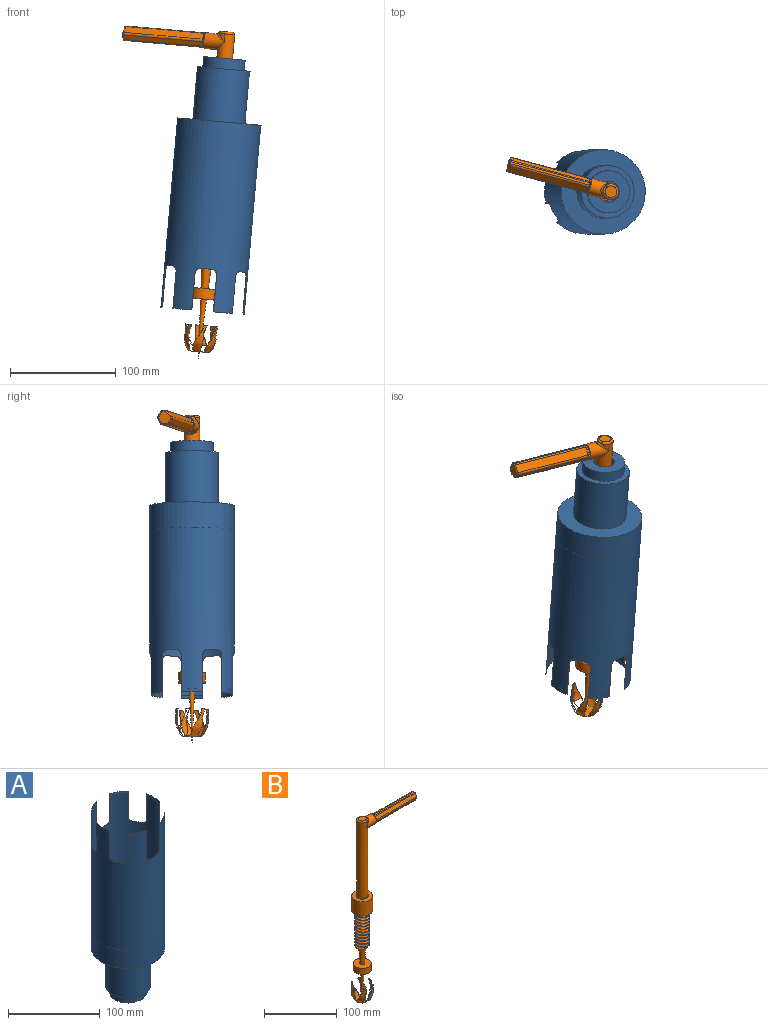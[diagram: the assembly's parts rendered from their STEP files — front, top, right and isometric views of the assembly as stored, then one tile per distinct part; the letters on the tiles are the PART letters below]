
ASSEMBLY  parts=2 mates=1
PART A: 54 faces, bbox 93.2x90.1x245.5 mm
  f0: plane 51.91x51.91mm, normal (0,0,1), area 1606.4mm2, adj f42,f44,f46,f47
  f1: cylinder r=39.5mm len=153.01mm, axis (0,0,-1), area 33532.5mm2, adj f4,f5,f6,f7,f8,f9,f10,f11
  f2: cylinder r=40mm len=180mm, axis (0,0,-1), area 40362.7mm2, adj f3,f4,f5,f6,f7,f8,f9,f10
  f3: plane 80x80mm, normal (0,0,-1), area 3063mm2, adj f2,f48
  f4: plane 35x0.35mm, normal (0.71,-0.71,0), area 17mm2, adj f1,f2,f25,f34
  f5: plane 35x0.48mm, normal (-0.26,0.97,0), area 17mm2, adj f1,f2,f26,f35
  f6: plane 9.56x5.8mm, normal (0,0,1), area 5.4mm2, adj f1,f2,f34,f35
  f7: plane 35x0.48mm, normal (-0.26,-0.97,0), area 17mm2, adj f1,f2,f26,f36
  f8: plane 35x0.35mm, normal (0.71,0.71,0), area 17mm2, adj f1,f2,f22,f37
  f9: plane 9.56x5.8mm, normal (0,0,1), area 5.4mm2, adj f1,f2,f36,f37
  f10: plane 35x0.48mm, normal (-0.97,-0.26,0), area 17mm2, adj f1,f2,f22,f38
  f11: plane 35x0.48mm, normal (0.97,-0.26,0), area 17mm2, adj f1,f2,f23,f39
  f12: plane 10.88x0.86mm, normal (0,0,1), area 5.4mm2, adj f1,f2,f38,f39
  f13: plane 35x0.35mm, normal (-0.71,0.71,0), area 17mm2, adj f1,f2,f23,f29
  f14: plane 35x0.48mm, normal (0.26,-0.97,0), area 17mm2, adj f1,f2,f27,f28
  f15: plane 9.56x5.8mm, normal (0,0,1), area 5.4mm2, adj f1,f2,f28,f29
  f16: plane 35x0.48mm, normal (0.26,0.97,0), area 17mm2, adj f1,f2,f27,f30
  f17: plane 35x0.35mm, normal (-0.71,-0.71,0), area 17mm2, adj f1,f2,f24,f31
  f18: plane 9.56x5.8mm, normal (0,0,1), area 5.4mm2, adj f1,f2,f30,f31
  f19: plane 35x0.48mm, normal (0.97,0.26,0), area 17mm2, adj f1,f2,f24,f32
  f20: plane 35x0.48mm, normal (-0.97,0.26,0), area 17mm2, adj f1,f2,f25,f33
  f21: plane 10.88x0.86mm, normal (0,0,1), area 5.4mm2, adj f1,f2,f32,f33
  f22: torus R=48.7mm, axis (0,0,1), area 63.3mm2, adj f1,f2,f8,f10
  f23: torus R=48.7mm, axis (0,0,1), area 63.3mm2, adj f1,f2,f11,f13
  f24: torus R=48.7mm, axis (0,0,1), area 63.3mm2, adj f1,f2,f17,f19
  f25: torus R=48.7mm, axis (0,0,1), area 63.3mm2, adj f1,f2,f4,f20
  f26: torus R=48.7mm, axis (0,0,1), area 63.3mm2, adj f1,f2,f5,f7
  f27: torus R=48.7mm, axis (0,0,1), area 63.3mm2, adj f1,f2,f14,f16
  f28: cylinder r=5mm len=5.04mm, axis (-0.97,-0.26,0), area 3.9mm2, adj f1,f2,f14,f15
  f29: cylinder r=5mm len=5mm, axis (0.71,0.71,0), area 3.9mm2, adj f1,f2,f13,f15
  f30: cylinder r=5mm len=5.04mm, axis (0.97,-0.26,0), area 3.9mm2, adj f1,f2,f16,f18
  f31: cylinder r=5mm len=5mm, axis (-0.71,0.71,0), area 3.9mm2, adj f1,f2,f17,f18
  f32: cylinder r=5mm len=5.04mm, axis (0.26,-0.97,0), area 3.9mm2, adj f1,f2,f19,f21
  f33: cylinder r=5mm len=5.04mm, axis (0.26,0.97,0), area 3.9mm2, adj f1,f2,f20,f21
  f34: cylinder r=5mm len=5mm, axis (-0.71,-0.71,0), area 3.9mm2, adj f1,f2,f4,f6
  f35: cylinder r=5mm len=5.04mm, axis (0.97,0.26,0), area 3.9mm2, adj f1,f2,f5,f6
  f36: cylinder r=5mm len=5.04mm, axis (-0.97,0.26,0), area 3.9mm2, adj f1,f2,f7,f9
  f37: cylinder r=5mm len=5mm, axis (0.71,-0.71,0), area 3.9mm2, adj f1,f2,f8,f9
  f38: cylinder r=5mm len=5.04mm, axis (-0.26,0.97,0), area 3.9mm2, adj f1,f2,f10,f12
  f39: cylinder r=5mm len=5.04mm, axis (-0.26,-0.97,0), area 3.9mm2, adj f1,f2,f11,f12
  f40: plane 79x79mm, normal (0,0,1), area 2938.2mm2, adj f1,f42
  f41: cylinder r=15mm len=74mm, axis (0,0,-1), area 6974.3mm2, adj f43,f52
  f42: cylinder r=25mm len=60mm, axis (0,0,-1), area 9424.8mm2, adj f0,f40
  f43: plane 31.91x31.91mm, normal (0,0,-1), area 349.8mm2, adj f41,f44,f45,f47
  f44: cylinder r=10mm len=60mm, axis (0,0,1), area 916.9mm2, adj f0,f43,f45,f46,f47
  f45: plane 2.57x2.57mm, normal (0,1,0), area 3.1mm2, adj f43,f44,f47
  f46: plane 2.57x2.57mm, normal (0,-1,0), area 3.1mm2, adj f0,f44,f47
  f47: bspline ~64x32.33mm, area 5274.5mm2, adj f0,f43,f44,f45,f46
  f48: cylinder r=25mm len=50mm, axis (0,0,1), area 7854mm2, adj f3,f49
  f49: plane 50x50mm, normal (0,0,-1), area 706.9mm2, adj f48,f50
  f50: cylinder r=20mm len=40mm, axis (0,0,1), area 1256.6mm2, adj f49,f51
  f51: plane 40x40mm, normal (0,0,-1), area 942.5mm2, adj f50,f53
  f52: plane 30x30mm, normal (0,0,1), area 392.7mm2, adj f41,f53
  f53: cylinder r=10mm len=20mm, axis (0,0,-1), area 628.3mm2, adj f51,f52
PART B: 83 faces, bbox 123x42.3x312.1 mm
  f0: cylinder r=10mm len=60mm, axis (0,0,1), area 916.9mm2, adj f1,f54,f55,f56,f82
  f1: plane 30.91x30.91mm, normal (0,0,-1), area 303.5mm2, adj f0,f2,f54,f55
  f2: cylinder r=14.5mm len=29mm, axis (0,0,-1), area 2186.5mm2, adj f1,f3
  f3: plane 29x29mm, normal (0,0,1), area 433.5mm2, adj f2,f4
  f4: torus R=8.5mm, axis (0,0,1), area 77.6mm2, adj f3,f5
  f5: cylinder r=7.5mm len=127mm, axis (0,0,-1), area 5698.8mm2, adj f4,f6,f7,f10,f52,f53
  f6: cylinder r=7.5mm len=8mm, axis (0,0,-1), area 30mm2, adj f5,f7,f10
  f7: torus R=5.5mm, axis (0,0,1), area 109.5mm2, adj f5,f6,f8,f9
  f8: plane 11.29x11mm, normal (0,0,1), area 95.9mm2, adj f7,f9
  f9: bspline ~10x3.52mm, area 20.6mm2, adj f7,f8,f10
  f10: bspline ~15x9.5mm, area 48.1mm2, adj f5,f6,f9,f11
  f11: cylinder r=7.5mm len=20mm, axis (-1,0,0), area 672.5mm2, adj f10,f12,f39,f40,f41,f42,f43,f44
  f12: bspline ~2.02x1.02mm, area 2mm2, adj f11,f13,f39,f51
  f13: plane 78.12x2.02mm, normal (0,-0.24,0.97), area 162.1mm2, adj f12,f14,f37,f38
  f14: cylinder r=2mm len=78.05mm, axis (1,0,0), area 162.9mm2, adj f13,f15,f36,f51
  f15: plane 77.23x5.6mm, normal (0,0.72,0.7), area 600.5mm2, adj f14,f16,f17,f35,f48,f50
  f16: cylinder r=2mm len=3.36mm, axis (0,0.7,-0.72), area 8.6mm2, adj f15,f48,f49,f50
  f17: cylinder r=2mm len=77.68mm, axis (1,0,0), area 200.8mm2, adj f15,f18,f34,f47
  f18: plane 77.56x4.18mm, normal (0,0.86,-0.5), area 373.7mm2, adj f17,f19,f33,f46
  f19: cylinder r=2mm len=77.93mm, axis (-1,0,0), area 162.8mm2, adj f18,f20,f32,f45
  f20: plane 77.56x5.19mm, normal (0,0,-1), area 401.5mm2, adj f19,f21,f31,f44
  f21: cylinder r=2mm len=77.93mm, axis (-1,0,0), area 162.8mm2, adj f20,f22,f30,f43
  f22: plane 77.56x4.51mm, normal (0,-0.87,-0.5), area 401.5mm2, adj f21,f23,f29,f42
  f23: cylinder r=2mm len=77.93mm, axis (1,0,0), area 162.8mm2, adj f22,f24,f28,f41
  f24: plane 77.65x4.76mm, normal (0,-0.86,0.5), area 425.6mm2, adj f23,f25,f38,f40
  f25: cylinder r=1mm len=5.26mm, axis (0,-0.5,-0.86), area 8.6mm2, adj f24,f26,f27,f28
  f26: torus R=1mm, axis (1,0,0), area 2.1mm2, adj f25,f27,f37,f38
  f27: plane 12.2x11.78mm, normal (1,0,0), area 98.9mm2, adj f25,f26,f28,f29,f30,f31,f32,f33
  f28: torus R=1mm, axis (1,0,0), area 2.7mm2, adj f23,f25,f27,f29
  f29: cylinder r=1mm len=5mm, axis (0,0.5,-0.87), area 8.2mm2, adj f22,f27,f28,f30
  f30: torus R=1mm, axis (1,0,0), area 2.7mm2, adj f21,f27,f29,f31
  f31: cylinder r=1mm len=5.19mm, axis (0,1,0), area 8.2mm2, adj f20,f27,f30,f32
  f32: torus R=1mm, axis (1,0,0), area 2.7mm2, adj f19,f27,f31,f33
  f33: cylinder r=1mm len=4.68mm, axis (0,0.5,0.86), area 7.6mm2, adj f18,f27,f32,f34
  f34: torus R=1mm, axis (1,0,0), area 3.3mm2, adj f17,f27,f33,f35
  f35: cylinder r=1mm len=6.3mm, axis (0,-0.7,0.72), area 12.2mm2, adj f15,f27,f34,f36
  f36: torus R=1mm, axis (1,0,0), area 2.7mm2, adj f14,f27,f35,f37
  f37: cylinder r=1mm len=2.26mm, axis (0,-0.97,-0.24), area 3.3mm2, adj f13,f26,f27,f36
  f38: cylinder r=2mm len=78.21mm, axis (1,0,0), area 124.7mm2, adj f13,f24,f26,f39
  f39: bspline ~2.73x1.73mm, area 2.1mm2, adj f11,f12,f38,f40
  f40: bspline ~4.76x3.15mm, area 9.8mm2, adj f11,f24,f39,f41
  f41: bspline ~3.87x1.55mm, area 3.6mm2, adj f11,f23,f40,f42
  f42: bspline ~4.5x2.97mm, area 9.4mm2, adj f11,f22,f41,f43
  f43: bspline ~3.33x2.16mm, area 3.6mm2, adj f11,f21,f42,f44
  f44: bspline ~5.19x1.73mm, area 9.4mm2, adj f11,f20,f43,f45
  f45: bspline ~3.37x2.09mm, area 3.6mm2, adj f11,f19,f44,f46
  f46: bspline ~4.18x2.92mm, area 8.8mm2, adj f11,f18,f45,f47
  f47: bspline ~5.31x1.96mm, area 5.6mm2, adj f11,f17,f46,f48
  f48: bspline ~3.08x2.35mm, area 6.1mm2, adj f11,f15,f16,f47
  f49: plane 1.97x1.9mm, normal (1,0,0), area 0.2mm2, adj f11,f16
  f50: bspline ~3.99x2.97mm, area 6.8mm2, adj f11,f15,f16,f51
  f51: bspline ~4.17x1.92mm, area 3.6mm2, adj f11,f12,f14,f50
  f52: bspline ~8.5x8.5mm, area 4.9mm2, adj f5,f11
  f53: bspline ~8.5x8.5mm, area 4.9mm2, adj f5,f11
  f54: plane 4.57x4.57mm, normal (0,1,0), area 9.4mm2, adj f0,f1,f55
  f55: bspline ~64x23.99mm, area 4151.6mm2, adj f0,f1,f54,f56,f82
  f56: plane 22.11x20.58mm, normal (0,0,-1), area 199.4mm2, adj f0,f55,f57,f82
  f57: cone r=5mm half-angle=3deg, axis (0,0,1), area 796.3mm2, adj f56,f58
  f58: plane 25x25mm, normal (0,0,1), area 453.8mm2, adj f57,f59
  f59: cylinder r=12.5mm len=25mm, axis (0,0,-1), area 785.4mm2, adj f58,f60
  f60: revolved ~50x31.19mm, area 3586.1mm2, adj f59,f61,f62,f63,f64,f65,f66,f67
  f61: bspline ~25x13.15mm, area 24.9mm2, adj f60,f77,f81
  f62: bspline ~25x12.66mm, area 26.6mm2, adj f60,f63,f77
  f63: plane 3.72x2.82mm, normal (0,0,-1), area 4.5mm2, adj f60,f62,f64,f77
  f64: bspline ~25x9.09mm, area 26.8mm2, adj f60,f63,f77
  f65: bspline ~25x13.31mm, area 26.5mm2, adj f60,f66,f77
  f66: plane 3.71x2.81mm, normal (0,0,-1), area 4.5mm2, adj f60,f65,f67,f77
  f67: bspline ~25x7.01mm, area 23.9mm2, adj f60,f66,f77
  f68: bspline ~25x17.08mm, area 26.9mm2, adj f60,f69,f77
  f69: plane 4.01x1.31mm, normal (0,0,-1), area 4.5mm2, adj f60,f68,f70,f77
  f70: bspline ~25x16.98mm, area 24.9mm2, adj f60,f69,f77
  f71: bspline ~25x15.24mm, area 26.9mm2, adj f60,f72,f77
  f72: plane 3.7x2.8mm, normal (0,0,-1), area 4.5mm2, adj f60,f71,f73,f77
  f73: bspline ~25x14.31mm, area 24.9mm2, adj f60,f72,f77
  f74: bspline ~25x16.77mm, area 26.9mm2, adj f60,f75,f77
  f75: plane 3.7x2.8mm, normal (0,0,-1), area 4.5mm2, adj f60,f74,f76,f77
  f76: bspline ~25x16.77mm, area 24.9mm2, adj f60,f75,f77
  f77: revolved ~50x28.84mm, area 3290.9mm2, adj f60,f61,f62,f63,f64,f65,f66,f67
  f78: plane 23x23mm, normal (0,0,-1), area 388.8mm2, adj f77,f79
  f79: cone r=5mm half-angle=3deg, axis (0,0,1), area 513.8mm2, adj f78
  f80: bspline ~25x17.01mm, area 27.1mm2, adj f60,f77,f81
  f81: plane 4.03x1.33mm, normal (0,0,-1), area 4.5mm2, adj f60,f61,f77,f80
  f82: plane 2.57x2.57mm, normal (0,-1,0), area 3.1mm2, adj f0,f55,f56
PLACE A rot(axis=(0,-1,0),175deg) t=(208.93,388.73,-68.64)mm
PLACE B rot(axis=(0.04,0.01,1),165deg) t=(202.94,388.73,-137.13)mm
MATE cylindrical B.f2 <-> A.f41  axis (-0.09,0,-1) through (203.99,388.73,-125.17)mm
